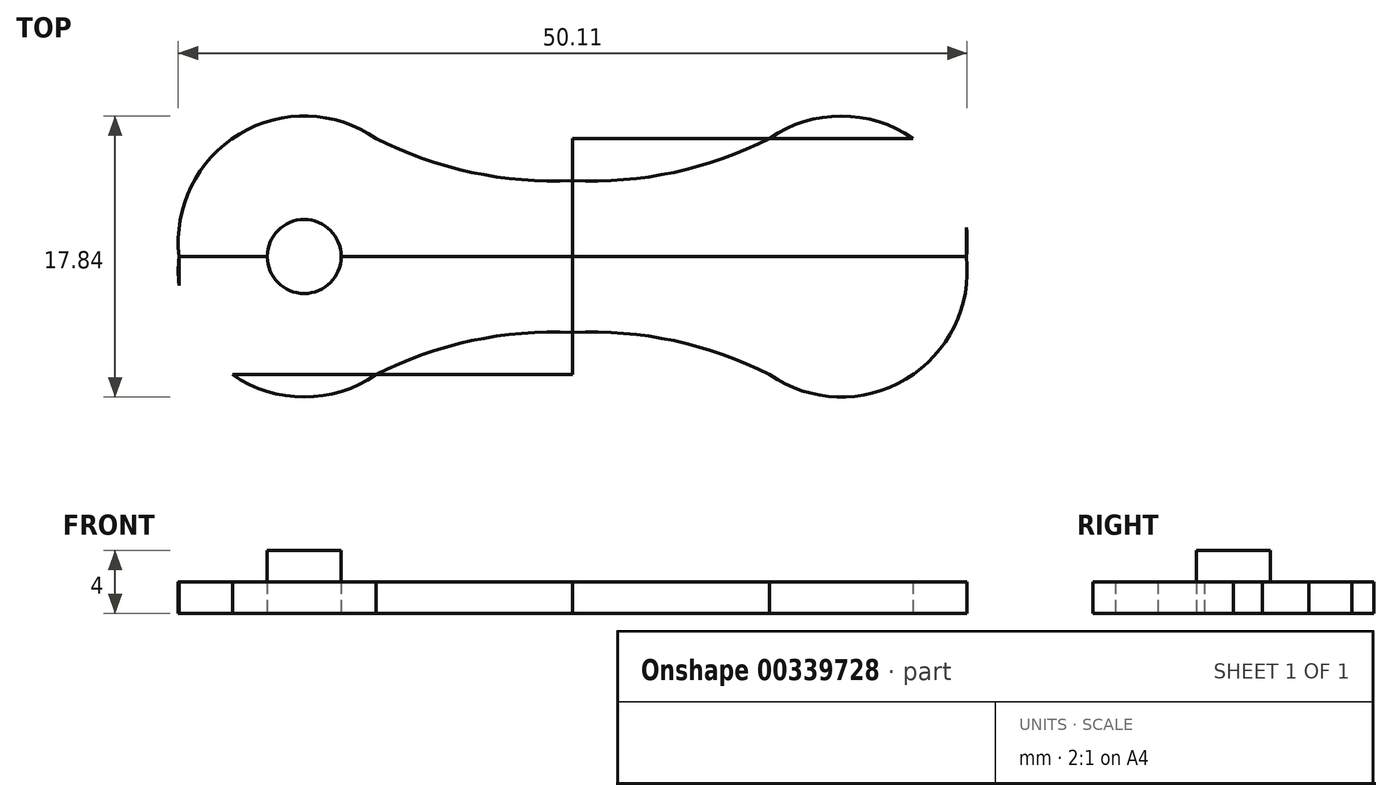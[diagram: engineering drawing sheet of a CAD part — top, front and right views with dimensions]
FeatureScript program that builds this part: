
annotation { "Feature Type Name" : "Feature", "Feature Type Description" : "" }
export const myFeature = defineFeature(function(context is Context, id is Id, definition is map)
    precondition{}
    {
        {
            var Q0;
            Q0=qCreatedBy(makeId("Top.planeOp"),FACE);
            var sketch = newSketch(context, id + "F0", { "sketchPlane" : qUnion([Q0])});
            skLineSegment(sketch, "E0.bottom", {"start": v(21.47, 6.05) * mm, "end": v(-28.53, 6.05) * mm});
            skLineSegment(sketch, "E0.top", {"start": v(21.47, -8.95) * mm, "end": v(-28.53, -8.95) * mm});
            skLineSegment(sketch, "E0.left", {"start": v(21.47, 6.05) * mm, "end": v(21.47, -8.95) * mm});
            skLineSegment(sketch, "E0.right", {"start": v(-28.53, 6.05) * mm, "end": v(-28.53, -8.95) * mm});
            skPoint(sketch, "E0.middle", {"position": v(-3.53, -1.45) * mm});
            skLineSegment(sketch, "E1", {"start": v(-3.53, -8.95) * mm, "end": v(-3.53, 6.05) * mm});
            skPoint(sketch, "E2", {"position": v(-16.03, 6.05) * mm});
            skArc(sketch, "E3", {"start": v(-16.03, 6.05) * mm, "mid": v(-24.7, 6.33) * mm, "end": v(-28.53, -1.45) * mm});
            skPoint(sketch, "E4", {"position": v(-3.53, 3.37) * mm});
            skLineSegment(sketch, "E5", {"start": v(-28.53, -1.45) * mm, "end": v(21.47, -1.45) * mm});
            skArc(sketch, "E6.MirrorCS", {"start": v(-16.03, -8.95) * mm, "mid": v(-24.7, -9.23) * mm, "end": v(-28.53, -1.45) * mm});
            skPoint(sketch, "E7.MirrorP", {"position": v(-3.53, -6.27) * mm});
            skArc(sketch, "E8", {"start": v(-16.03, 6.05) * mm, "mid": v(-9.96, 3.9) * mm, "end": v(-3.53, 3.37) * mm});
            skArc(sketch, "E9.MirrorCS", {"start": v(8.97, 6.05) * mm, "mid": v(2.9, 3.9) * mm, "end": v(-3.53, 3.37) * mm});
            skArc(sketch, "E10.MirrorCS", {"start": v(8.97, 6.05) * mm, "mid": v(17.64, 6.33) * mm, "end": v(21.47, -1.45) * mm});
            skArc(sketch, "E11.MirrorCS", {"start": v(8.97, -8.95) * mm, "mid": v(17.64, -9.23) * mm, "end": v(21.47, -1.45) * mm});
            skArc(sketch, "E12.MirrorCS", {"start": v(-16.03, -8.95) * mm, "mid": v(-9.96, -6.8) * mm, "end": v(-3.53, -6.27) * mm});
            skArc(sketch, "E13.MirrorCS", {"start": v(8.97, -8.95) * mm, "mid": v(2.9, -6.8) * mm, "end": v(-3.53, -6.27) * mm});
            skLineSegment(sketch, "E14", {"start": v(-20.59, -0.53) * mm, "end": v(-20.59, -2.37) * mm});
            skCircle(sketch, "E15", {"center": v(-20.59, -1.45) * mm, "radius": 2.35 * mm});
            skSolve(sketch);
        }
        {
            var Q0;
            {var subQ5=sQuery(id+"F0.wireOp",EDGE,"E8");Q0=makeQuery(id+"F0.imprint","IMPRINT",FACE,{"disambiguationData":[TD([[makeQuery(id+"F0.imprint","IMPRINT",EDGE,{"derivedFrom":subQ5}),-1.0]])]});}
            var Q1;
            {var subQ0=sQuery(id+"F0.wireOp",EDGE,"E3");var subQ1=sQuery(id+"F0.wireOp",EDGE,"E0.bottom");var subQ3=makeQuery(id+"F0.imprint","INTERSECT",VERTEX,{"derivedFrom":[subQ1,subQ0]});Q1=makeQuery(id+"F0.imprint","IMPRINT",FACE,{"disambiguationData":[TD([[makeQuery(id+"F0.imprint","IMPRINT",EDGE,{"disambiguationData":[TD([[subQ3,1.0]])],"derivedFrom":subQ1}),-1.0]])]});}
            var Q2;
            {var subQ6=sQuery(id+"F0.wireOp",EDGE,"E12.MirrorCS");Q2=makeQuery(id+"F0.imprint","IMPRINT",FACE,{"disambiguationData":[TD([[makeQuery(id+"F0.imprint","IMPRINT",EDGE,{"derivedFrom":subQ6}),1.0]])]});}
            var Q3;
            {var subQ0=sQuery(id+"F0.wireOp",EDGE,"E6.MirrorCS");var subQ1=sQuery(id+"F0.wireOp",EDGE,"E0.top");var subQ3=makeQuery(id+"F0.imprint","INTERSECT",VERTEX,{"derivedFrom":[subQ1,subQ0]});Q3=makeQuery(id+"F0.imprint","IMPRINT",FACE,{"disambiguationData":[TD([[makeQuery(id+"F0.imprint","IMPRINT",EDGE,{"disambiguationData":[TD([[subQ3,1.0]])],"derivedFrom":subQ1}),1.0]])]});}
            var Q4;
            {var subQ0=sQuery(id+"F0.wireOp",EDGE,"E11.MirrorCS");var subQ1=sQuery(id+"F0.wireOp",EDGE,"E0.top");var subQ3=makeQuery(id+"F0.imprint","INTERSECT",VERTEX,{"derivedFrom":[subQ1,subQ0]});Q4=makeQuery(id+"F0.imprint","IMPRINT",FACE,{"disambiguationData":[TD([[makeQuery(id+"F0.imprint","IMPRINT",EDGE,{"disambiguationData":[TD([[subQ3,-1.0]])],"derivedFrom":subQ1}),1.0]])]});}
            var Q5;
            {var subQ6=sQuery(id+"F0.wireOp",EDGE,"E13.MirrorCS");Q5=makeQuery(id+"F0.imprint","IMPRINT",FACE,{"disambiguationData":[TD([[makeQuery(id+"F0.imprint","IMPRINT",EDGE,{"derivedFrom":subQ6}),-1.0]])]});}
            var Q6;
            {var subQ0=sQuery(id+"F0.wireOp",EDGE,"E9.MirrorCS");Q6=makeQuery(id+"F0.imprint","IMPRINT",FACE,{"disambiguationData":[TD([[makeQuery(id+"F0.imprint","IMPRINT",EDGE,{"derivedFrom":subQ0}),1.0]])]});}
            var Q7;
            {var subQ0=sQuery(id+"F0.wireOp",EDGE,"E3");var subQ1=sQuery(id+"F0.wireOp",EDGE,"E0.right");var subQ3=makeQuery(id+"F0.imprint","INTERSECT",VERTEX,{"derivedFrom":[subQ1,subQ0]});Q7=makeQuery(id+"F0.imprint","IMPRINT",FACE,{"disambiguationData":[TD([[makeQuery(id+"F0.imprint","IMPRINT",EDGE,{"disambiguationData":[TD([[subQ3,-1.0]])],"derivedFrom":subQ1}),-1.0]])]});}
            var Q8;
            {var subQ0=sQuery(id+"F0.wireOp",EDGE,"E6.MirrorCS");var subQ1=sQuery(id+"F0.wireOp",EDGE,"E0.right");var subQ3=makeQuery(id+"F0.imprint","INTERSECT",VERTEX,{"derivedFrom":[subQ1,subQ0]});Q8=makeQuery(id+"F0.imprint","IMPRINT",FACE,{"disambiguationData":[TD([[makeQuery(id+"F0.imprint","IMPRINT",EDGE,{"disambiguationData":[TD([[subQ3,1.0]])],"derivedFrom":subQ1}),-1.0]])]});}
            var Q9;
            {var subQ0=sQuery(id+"F0.wireOp",EDGE,"E11.MirrorCS");var subQ1=sQuery(id+"F0.wireOp",EDGE,"E0.left");var subQ3=makeQuery(id+"F0.imprint","INTERSECT",VERTEX,{"derivedFrom":[subQ1,subQ0]});Q9=makeQuery(id+"F0.imprint","IMPRINT",FACE,{"disambiguationData":[TD([[makeQuery(id+"F0.imprint","IMPRINT",EDGE,{"disambiguationData":[TD([[subQ3,1.0]])],"derivedFrom":subQ1}),1.0]])]});}
            var Q10;
            {var subQ0=sQuery(id+"F0.wireOp",EDGE,"E10.MirrorCS");var subQ1=sQuery(id+"F0.wireOp",EDGE,"E0.left");var subQ3=makeQuery(id+"F0.imprint","INTERSECT",VERTEX,{"derivedFrom":[subQ1,subQ0]});Q10=makeQuery(id+"F0.imprint","IMPRINT",FACE,{"disambiguationData":[TD([[makeQuery(id+"F0.imprint","IMPRINT",EDGE,{"disambiguationData":[TD([[subQ3,-1.0]])],"derivedFrom":subQ1}),1.0]])]});}
            var Q11;
            {var subQ0=sQuery(id+"F0.wireOp",EDGE,"E10.MirrorCS");var subQ1=sQuery(id+"F0.wireOp",EDGE,"E0.bottom");var subQ3=makeQuery(id+"F0.imprint","INTERSECT",VERTEX,{"derivedFrom":[subQ1,subQ0]});Q11=makeQuery(id+"F0.imprint","IMPRINT",FACE,{"disambiguationData":[TD([[makeQuery(id+"F0.imprint","IMPRINT",EDGE,{"disambiguationData":[TD([[subQ3,-1.0]])],"derivedFrom":subQ1}),-1.0]])]});}
            extrude(context, id + "F1", {"entities" : qUnion([Q0, Q1, Q2, Q3, Q4, Q5, Q6, Q7, Q8, Q9, Q10, Q11]), "depth" : 2 * mm});
        }
        {
            var Q0;
            {var subQ0=sQuery(id+"F0.wireOp",EDGE,"E5");var subQ1=makeQuery(id+"F0.imprint","IMPRINT",VERTEX,{"derivedFrom":subQ0});Q0=makeQuery(id+"F0.imprint","IMPRINT",FACE,{"disambiguationData":[TD([[makeQuery(id+"F0.imprint","IMPRINT",EDGE,{"disambiguationData":[TD([[subQ1,1.0]])],"derivedFrom":subQ0}),1.0]])]});}
            var Q1;
            {var subQ0=sQuery(id+"F0.wireOp",EDGE,"E5");var subQ1=makeQuery(id+"F0.imprint","IMPRINT",VERTEX,{"derivedFrom":subQ0});Q1=makeQuery(id+"F0.imprint","IMPRINT",FACE,{"disambiguationData":[TD([[makeQuery(id+"F0.imprint","IMPRINT",EDGE,{"disambiguationData":[TD([[subQ1,1.0]])],"derivedFrom":subQ0}),-1.0]])]});}
            extrude(context, id + "F2", {"entities" : qUnion([Q0, Q1]), "operationType" : NewBodyOperationType.ADD, "depth" : 4 * mm});
        }
    });
